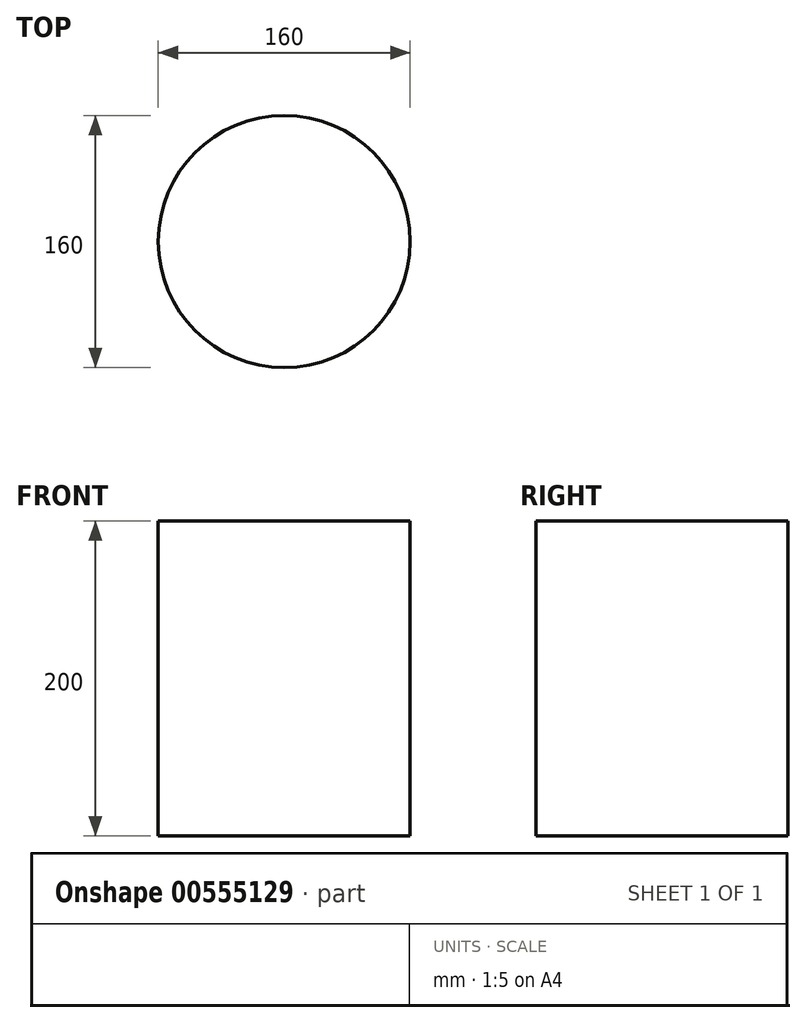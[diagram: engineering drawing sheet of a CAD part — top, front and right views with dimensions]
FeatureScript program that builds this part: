
annotation { "Feature Type Name" : "Feature", "Feature Type Description" : "" }
export const myFeature = defineFeature(function(context is Context, id is Id, definition is map)
    precondition{}
    {
        {
            var Q0;
            Q0=qCreatedBy(makeId("Top.planeOp"),FACE);
            var sketch = newSketch(context, id + "F0", { "sketchPlane" : qUnion([Q0])});
            skCircle(sketch, "E0", {"center": v(0, 0) * mm, "radius": 80 * mm});
            skSolve(sketch);
        }
        {
            var Q0;
            Q0 = qSketchRegion(id + "F0", true);
            extrude(context, id + "F1", {"entities" : qUnion([Q0]), "depth" : 200 * mm, "offsetDistance" : 25 * mm});
        }
        {
            var Q0;
            Q0=makeQuery(id+"F1.opExtrude","SWEPT_BODY",BODY,{"disambiguationData":[OSD([sQuery(id+"F0.wireOp",EDGE,"E0")])]});
            transform(context, id + "F2", {"entities" : qUnion([Q0]), "transformType" : TransformType.TRANSLATION_3D, "dx" : 0 * mm, "dy" : 0 * mm, "dz" : 0 * mm, "makeCopy" : true});
        }
        {
            var Q0;
            Q0=makeQuery(id+"F2.opPattern","COPY",BODY,{"derivedFrom":makeQuery(id+"F1.opExtrude","SWEPT_BODY",BODY,{"disambiguationData":[OSD([sQuery(id+"F0.wireOp",EDGE,"E0")])]}),"instanceName":"1"});
            deleteBodies(context, id + "F3", {"entities" : qUnion([Q0])});
        }
    });
